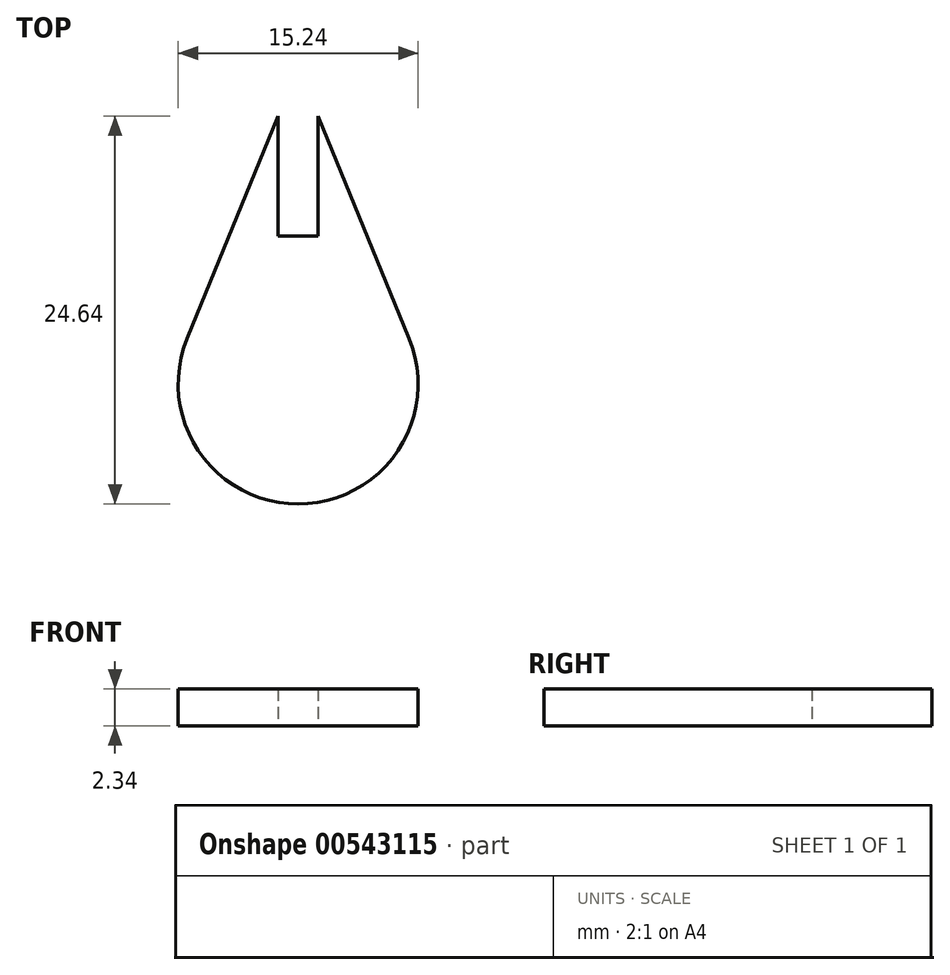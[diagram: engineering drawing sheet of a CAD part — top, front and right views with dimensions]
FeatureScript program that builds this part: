
annotation { "Feature Type Name" : "Feature", "Feature Type Description" : "" }
export const myFeature = defineFeature(function(context is Context, id is Id, definition is map)
    precondition{}
    {
        {
            var Q0;
            Q0=qCreatedBy(makeId("Top.planeOp"),FACE);
            var sketch = newSketch(context, id + "F0", { "sketchPlane" : qUnion([Q0])});
            skArc(sketch, "E0", {"start": v(-7.05, 2.89) * mm, "mid": v(0, -7.62) * mm, "end": v(7.05, 2.89) * mm});
            skLineSegment(sketch, "E1", {"start": v(-1.27, 17.02) * mm, "end": v(-1.27, 9.4) * mm});
            skLineSegment(sketch, "E2", {"start": v(-1.27, 17.02) * mm, "end": v(-7.05, 2.89) * mm});
            skLineSegment(sketch, "E3.trimOffspring", {"start": v(-1.27, 9.4) * mm, "end": v(1.27, 9.4) * mm});
            skLineSegment(sketch, "E4.MirrorCS", {"start": v(1.27, 17.02) * mm, "end": v(1.27, 9.4) * mm});
            skLineSegment(sketch, "E5.MirrorCS", {"start": v(1.27, 17.02) * mm, "end": v(7.05, 2.89) * mm});
            skSolve(sketch);
        }
        {
            var Q0;
            Q0=makeQuery(id+"F0.imprint","IMPRINT",FACE,{"disambiguationData":[TD([[makeQuery(id+"F0.imprint","IMPRINT",EDGE,{"derivedFrom":sQuery(id+"F0.wireOp",EDGE,"E0")}),1.0]])]});
            extrude(context, id + "F1", {"entities" : qUnion([Q0]), "depth" : 2.34 * mm, "offsetDistance" : 25.4 * mm});
        }
    });
